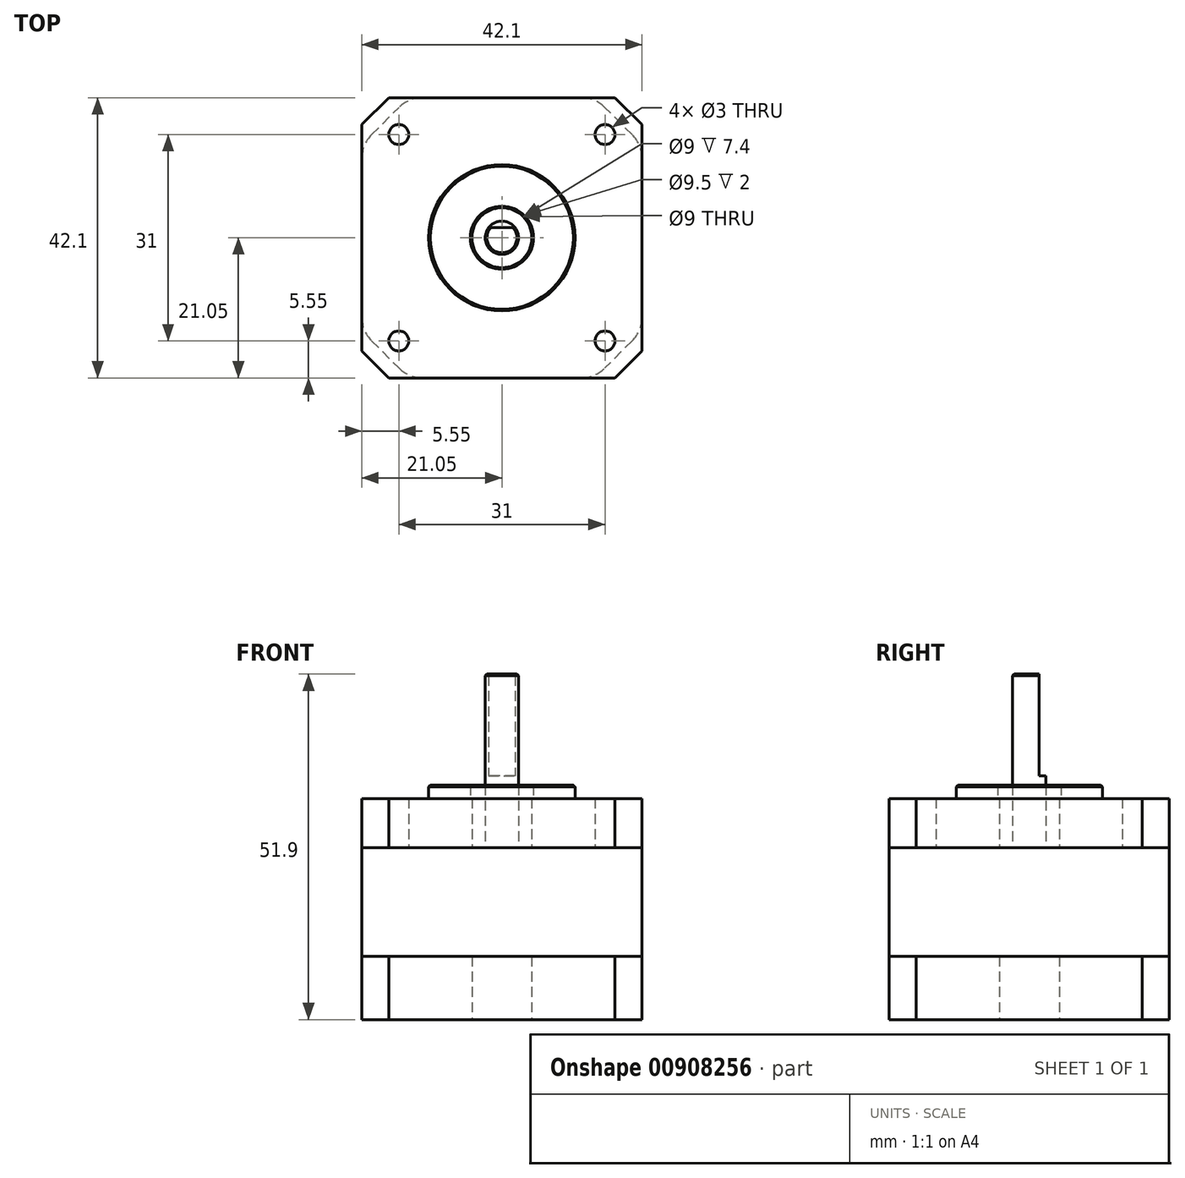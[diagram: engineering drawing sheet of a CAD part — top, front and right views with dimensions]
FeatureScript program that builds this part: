
annotation { "Feature Type Name" : "Feature", "Feature Type Description" : "" }
export const myFeature = defineFeature(function(context is Context, id is Id, definition is map)
    precondition{}
    {
        {
            var Q0;
            Q0=qCreatedBy(makeId("Top.planeOp"),FACE);
            var sketch = newSketch(context, id + "F0", { "sketchPlane" : qUnion([Q0])});
            skPoint(sketch, "E0.middle", {"position": v(0, 0) * mm});
            skLineSegment(sketch, "E1", {"start": v(0, 21.05) * mm, "end": v(17, 21.05) * mm});
            skLineSegment(sketch, "E2", {"start": v(17, 21.05) * mm, "end": v(21.05, 17) * mm});
            skLineSegment(sketch, "E3", {"start": v(21.05, 17) * mm, "end": v(21.05, 0) * mm});
            skLineSegment(sketch, "E4.MirrorCS", {"start": v(0, 21.05) * mm, "end": v(-17, 21.05) * mm});
            skLineSegment(sketch, "E5.MirrorCS", {"start": v(-21.05, 17) * mm, "end": v(-21.05, 0) * mm});
            skLineSegment(sketch, "E6.MirrorCS", {"start": v(-17, 21.05) * mm, "end": v(-21.05, 17) * mm});
            skLineSegment(sketch, "E7.MirrorCS", {"start": v(21.05, -17) * mm, "end": v(21.05, 0) * mm});
            skLineSegment(sketch, "E8.MirrorCS", {"start": v(17, -21.05) * mm, "end": v(21.05, -17) * mm});
            skLineSegment(sketch, "E9.MirrorCS", {"start": v(0, -21.05) * mm, "end": v(17, -21.05) * mm});
            skLineSegment(sketch, "E10.MirrorCS", {"start": v(0, -21.05) * mm, "end": v(-17, -21.05) * mm});
            skLineSegment(sketch, "E11.MirrorCS", {"start": v(-17, -21.05) * mm, "end": v(-21.05, -17) * mm});
            skLineSegment(sketch, "E12.MirrorCS", {"start": v(-21.05, -17) * mm, "end": v(-21.05, 0) * mm});
            skCircle(sketch, "E13", {"center": v(0, 0) * mm, "radius": 4.5 * mm});
            skSolve(sketch);
        }
        {
            var Q0;
            Q0 = qSketchRegion(id + "F0", true);
            extrude(context, id + "F1", {"entities" : qUnion([Q0]), "depth" : 9.5 * mm, "offsetDistance" : 25 * mm});
        }
        {
            var Q0;
            Q0=makeQuery(id+"F1.opExtrude","CAP_FACE",FACE,{"disambiguationData":[OSD([sQuery(id+"F0.wireOp",EDGE,"E1"),sQuery(id+"F0.wireOp",EDGE,"E4.MirrorCS"),sQuery(id+"F0.wireOp",EDGE,"E5.MirrorCS"),sQuery(id+"F0.wireOp",EDGE,"E6.MirrorCS"),sQuery(id+"F0.wireOp",EDGE,"E2"),sQuery(id+"F0.wireOp",EDGE,"E3"),sQuery(id+"F0.wireOp",EDGE,"E7.MirrorCS"),sQuery(id+"F0.wireOp",EDGE,"E8.MirrorCS"),sQuery(id+"F0.wireOp",EDGE,"E9.MirrorCS"),sQuery(id+"F0.wireOp",EDGE,"E10.MirrorCS"),sQuery(id+"F0.wireOp",EDGE,"E11.MirrorCS"),sQuery(id+"F0.wireOp",EDGE,"E12.MirrorCS"),sQuery(id+"F0.wireOp",EDGE,"E13")])],"isStart":false});
            var sketch = newSketch(context, id + "F2", { "sketchPlane" : qUnion([Q0])});
            skLineSegment(sketch, "E14", {"start": v(-21.05, 0) * mm, "end": v(-21.05, 14) * mm});
            skLineSegment(sketch, "E15", {"start": v(-21.05, 14) * mm, "end": v(-14, 21.05) * mm});
            skLineSegment(sketch, "E16", {"start": v(-14, 21.05) * mm, "end": v(0, 21.05) * mm});
            skLineSegment(sketch, "E17.MirrorCS", {"start": v(21.05, 0) * mm, "end": v(21.05, 14) * mm});
            skLineSegment(sketch, "E18.MirrorCS", {"start": v(21.05, 14) * mm, "end": v(14, 21.05) * mm});
            skLineSegment(sketch, "E19.MirrorCS", {"start": v(14, 21.05) * mm, "end": v(0, 21.05) * mm});
            skLineSegment(sketch, "E20.MirrorCS", {"start": v(21.05, 0) * mm, "end": v(21.05, -14) * mm});
            skLineSegment(sketch, "E21.MirrorCS", {"start": v(21.05, -14) * mm, "end": v(14, -21.05) * mm});
            skLineSegment(sketch, "E22.MirrorCS", {"start": v(14, -21.05) * mm, "end": v(0, -21.05) * mm});
            skLineSegment(sketch, "E23.MirrorCS", {"start": v(-14, -21.05) * mm, "end": v(0, -21.05) * mm});
            skLineSegment(sketch, "E24.MirrorCS", {"start": v(-21.05, -14) * mm, "end": v(-14, -21.05) * mm});
            skLineSegment(sketch, "E25.MirrorCS", {"start": v(-21.05, 0) * mm, "end": v(-21.05, -14) * mm});
            skSolve(sketch);
        }
        {
            var Q0;
            Q0 = qSketchRegion(id + "F2", true);
            extrude(context, id + "F3", {"entities" : qUnion([Q0]), "depth" : 16.3 * mm, "offsetDistance" : 25 * mm});
        }
        {
            var Q0;
            Q0=makeQuery(id+"F3.opExtrude","CAP_FACE",FACE,{"disambiguationData":[OSD([sQuery(id+"F2.wireOp",EDGE,"E14"),sQuery(id+"F2.wireOp",EDGE,"E15"),sQuery(id+"F2.wireOp",EDGE,"E16"),sQuery(id+"F2.wireOp",EDGE,"E17.MirrorCS"),sQuery(id+"F2.wireOp",EDGE,"E18.MirrorCS"),sQuery(id+"F2.wireOp",EDGE,"E19.MirrorCS"),sQuery(id+"F2.wireOp",EDGE,"E20.MirrorCS"),sQuery(id+"F2.wireOp",EDGE,"E21.MirrorCS"),sQuery(id+"F2.wireOp",EDGE,"E22.MirrorCS"),sQuery(id+"F2.wireOp",EDGE,"E23.MirrorCS"),sQuery(id+"F2.wireOp",EDGE,"E24.MirrorCS"),sQuery(id+"F2.wireOp",EDGE,"E25.MirrorCS")])],"isStart":false});
            var sketch = newSketch(context, id + "F4", { "sketchPlane" : qUnion([Q0])});
            skPoint(sketch, "E26.middle", {"position": v(0, 0) * mm});
            skLineSegment(sketch, "E27", {"start": v(0, 21.05) * mm, "end": v(17, 21.05) * mm});
            skLineSegment(sketch, "E28", {"start": v(17, 21.05) * mm, "end": v(21.05, 17) * mm});
            skLineSegment(sketch, "E29", {"start": v(21.05, 17) * mm, "end": v(21.05, 0) * mm});
            skLineSegment(sketch, "E30.MirrorCS", {"start": v(0, 21.05) * mm, "end": v(-17, 21.05) * mm});
            skLineSegment(sketch, "E31.MirrorCS", {"start": v(-21.05, 17) * mm, "end": v(-21.05, 0) * mm});
            skLineSegment(sketch, "E32.MirrorCS", {"start": v(-17, 21.05) * mm, "end": v(-21.05, 17) * mm});
            skLineSegment(sketch, "E33.MirrorCS", {"start": v(21.05, -17) * mm, "end": v(21.05, 0) * mm});
            skLineSegment(sketch, "E34.MirrorCS", {"start": v(17, -21.05) * mm, "end": v(21.05, -17) * mm});
            skLineSegment(sketch, "E35.MirrorCS", {"start": v(0, -21.05) * mm, "end": v(17, -21.05) * mm});
            skLineSegment(sketch, "E36.MirrorCS", {"start": v(0, -21.05) * mm, "end": v(-17, -21.05) * mm});
            skLineSegment(sketch, "E37.MirrorCS", {"start": v(-17, -21.05) * mm, "end": v(-21.05, -17) * mm});
            skLineSegment(sketch, "E38.MirrorCS", {"start": v(-21.05, -17) * mm, "end": v(-21.05, 0) * mm});
            skCircle(sketch, "E39", {"center": v(0, 0) * mm, "radius": 4.5 * mm});
            skCircle(sketch, "E40", {"center": v(15.5, 15.5) * mm, "radius": 1.5 * mm});
            skCircle(sketch, "E41.MirrorC", {"center": v(-15.5, 15.5) * mm, "radius": 1.5 * mm});
            skCircle(sketch, "E42.MirrorC", {"center": v(15.5, -15.5) * mm, "radius": 1.5 * mm});
            skCircle(sketch, "E43.MirrorC", {"center": v(-15.5, -15.5) * mm, "radius": 1.5 * mm});
            skSolve(sketch);
        }
        {
            var Q0;
            Q0 = qSketchRegion(id + "F4", true);
            extrude(context, id + "F5", {"entities" : qUnion([Q0]), "depth" : 7.4 * mm, "offsetDistance" : 25 * mm});
        }
        {
            var Q0;
            Q0=makeQuery(id+"F5.opExtrude","CAP_FACE",FACE,{"disambiguationData":[OSD([sQuery(id+"F4.wireOp",EDGE,"E27"),sQuery(id+"F4.wireOp",EDGE,"E30.MirrorCS"),sQuery(id+"F4.wireOp",EDGE,"E31.MirrorCS"),sQuery(id+"F4.wireOp",EDGE,"E32.MirrorCS"),sQuery(id+"F4.wireOp",EDGE,"E28"),sQuery(id+"F4.wireOp",EDGE,"E29"),sQuery(id+"F4.wireOp",EDGE,"E33.MirrorCS"),sQuery(id+"F4.wireOp",EDGE,"E34.MirrorCS"),sQuery(id+"F4.wireOp",EDGE,"E35.MirrorCS"),sQuery(id+"F4.wireOp",EDGE,"E36.MirrorCS"),sQuery(id+"F4.wireOp",EDGE,"E37.MirrorCS"),sQuery(id+"F4.wireOp",EDGE,"E38.MirrorCS"),sQuery(id+"F4.wireOp",EDGE,"E39"),sQuery(id+"F4.wireOp",EDGE,"E40"),sQuery(id+"F4.wireOp",EDGE,"E41.MirrorC"),sQuery(id+"F4.wireOp",EDGE,"E42.MirrorC"),sQuery(id+"F4.wireOp",EDGE,"E43.MirrorC")])],"isStart":false});
            var sketch = newSketch(context, id + "F6", { "sketchPlane" : qUnion([Q0])});
            skCircle(sketch, "E44", {"center": v(0, 0) * mm, "radius": 11 * mm});
            skCircle(sketch, "E45", {"center": v(0, 0) * mm, "radius": 4.75 * mm});
            skSolve(sketch);
        }
        {
            var Q0;
            Q0 = qSketchRegion(id + "F6", true);
            extrude(context, id + "F7", {"entities" : qUnion([Q0]), "operationType" : NewBodyOperationType.ADD, "depth" : 2 * mm, "offsetDistance" : 25 * mm});
        }
        {
            var Q0;
            Q0=makeQuery(id+"F7.opExtrude","CAP_EDGE",EDGE,{"disambiguationData":[OSD([sQuery(id+"F6.wireOp",EDGE,"E44")])],"isStart":false});
            chamfer(context, id + "F8", {"entities" : qUnion([Q0]), "width" : 0.25 * mm, "tangentPropagation" : true});
        }
        {
            var Q0;
            Q0=makeQuery(id+"F3.opExtrude","CAP_FACE",FACE,{"disambiguationData":[OSD([sQuery(id+"F2.wireOp",EDGE,"E14"),sQuery(id+"F2.wireOp",EDGE,"E15"),sQuery(id+"F2.wireOp",EDGE,"E16"),sQuery(id+"F2.wireOp",EDGE,"E17.MirrorCS"),sQuery(id+"F2.wireOp",EDGE,"E18.MirrorCS"),sQuery(id+"F2.wireOp",EDGE,"E19.MirrorCS"),sQuery(id+"F2.wireOp",EDGE,"E20.MirrorCS"),sQuery(id+"F2.wireOp",EDGE,"E21.MirrorCS"),sQuery(id+"F2.wireOp",EDGE,"E22.MirrorCS"),sQuery(id+"F2.wireOp",EDGE,"E23.MirrorCS"),sQuery(id+"F2.wireOp",EDGE,"E24.MirrorCS"),sQuery(id+"F2.wireOp",EDGE,"E25.MirrorCS")])],"isStart":false});
            var sketch = newSketch(context, id + "F9", { "sketchPlane" : qUnion([Q0])});
            skCircle(sketch, "E46", {"center": v(0, 0) * mm, "radius": 2.5 * mm});
            skSolve(sketch);
        }
        {
            var Q0;
            Q0 = qSketchRegion(id + "F9", true);
            extrude(context, id + "F10", {"entities" : qUnion([Q0]), "depth" : 26.1 * mm, "offsetDistance" : 25 * mm});
        }
        {
            var Q0;
            Q0=makeQuery(id+"F10.opExtrude","CAP_EDGE",EDGE,{"disambiguationData":[OSD([sQuery(id+"F9.wireOp",EDGE,"E46")])],"isStart":false});
            chamfer(context, id + "F11", {"entities" : qUnion([Q0]), "width" : 0.25 * mm, "tangentPropagation" : true});
        }
        {
            var Q0;
            Q0=makeQuery(id+"F10.opExtrude","CAP_FACE",FACE,{"disambiguationData":[OSD([sQuery(id+"F9.wireOp",EDGE,"E46")])],"isStart":false});
            var sketch = newSketch(context, id + "F12", { "sketchPlane" : qUnion([Q0])});
            skLineSegment(sketch, "E47.bottom", {"start": v(-3.24, 3.4) * mm, "end": v(3.22, 3.4) * mm});
            skLineSegment(sketch, "E47.top", {"start": v(-3.24, 1.5) * mm, "end": v(3.22, 1.5) * mm});
            skLineSegment(sketch, "E47.left", {"start": v(-3.24, 3.4) * mm, "end": v(-3.24, 1.5) * mm});
            skLineSegment(sketch, "E47.right", {"start": v(3.22, 3.4) * mm, "end": v(3.22, 1.5) * mm});
            skSolve(sketch);
        }
        {
            var Q0;
            Q0 = qSketchRegion(id + "F12", true);
            extrude(context, id + "F13", {"entities" : qUnion([Q0]), "operationType" : NewBodyOperationType.REMOVE, "oppositeDirection" : true, "depth" : 15.3 * mm, "offsetDistance" : 25 * mm});
        }
        {
            var Q0;
            Q0=makeQuery(id+"F3.opExtrude","SWEPT_EDGE",EDGE,{"disambiguationData":[OSD([sQuery(id+"F0.wireOp",EDGE,"E1"),sQuery(id+"F0.wireOp",EDGE,"E4.MirrorCS"),sQuery(id+"F2.wireOp",EDGE,"E18.MirrorCS"),sQuery(id+"F2.wireOp",EDGE,"E19.MirrorCS")])]});
            var Q1;
            Q1=makeQuery(id+"F3.opExtrude","SWEPT_EDGE",EDGE,{"disambiguationData":[OSD([sQuery(id+"F0.wireOp",EDGE,"E3"),sQuery(id+"F0.wireOp",EDGE,"E7.MirrorCS"),sQuery(id+"F2.wireOp",EDGE,"E17.MirrorCS"),sQuery(id+"F2.wireOp",EDGE,"E18.MirrorCS")])]});
            var Q2;
            Q2=makeQuery(id+"F3.opExtrude","SWEPT_EDGE",EDGE,{"disambiguationData":[OSD([sQuery(id+"F0.wireOp",EDGE,"E3"),sQuery(id+"F0.wireOp",EDGE,"E7.MirrorCS"),sQuery(id+"F2.wireOp",EDGE,"E20.MirrorCS"),sQuery(id+"F2.wireOp",EDGE,"E21.MirrorCS")])]});
            var Q3;
            Q3=makeQuery(id+"F3.opExtrude","SWEPT_EDGE",EDGE,{"disambiguationData":[OSD([sQuery(id+"F0.wireOp",EDGE,"E9.MirrorCS"),sQuery(id+"F0.wireOp",EDGE,"E10.MirrorCS"),sQuery(id+"F2.wireOp",EDGE,"E21.MirrorCS"),sQuery(id+"F2.wireOp",EDGE,"E22.MirrorCS")])]});
            var Q4;
            Q4=makeQuery(id+"F3.opExtrude","SWEPT_EDGE",EDGE,{"disambiguationData":[OSD([sQuery(id+"F0.wireOp",EDGE,"E9.MirrorCS"),sQuery(id+"F0.wireOp",EDGE,"E10.MirrorCS"),sQuery(id+"F2.wireOp",EDGE,"E23.MirrorCS"),sQuery(id+"F2.wireOp",EDGE,"E24.MirrorCS")])]});
            var Q5;
            Q5=makeQuery(id+"F3.opExtrude","SWEPT_EDGE",EDGE,{"disambiguationData":[OSD([sQuery(id+"F0.wireOp",EDGE,"E5.MirrorCS"),sQuery(id+"F0.wireOp",EDGE,"E12.MirrorCS"),sQuery(id+"F2.wireOp",EDGE,"E24.MirrorCS"),sQuery(id+"F2.wireOp",EDGE,"E25.MirrorCS")])]});
            var Q6;
            Q6=makeQuery(id+"F3.opExtrude","SWEPT_EDGE",EDGE,{"disambiguationData":[OSD([sQuery(id+"F0.wireOp",EDGE,"E5.MirrorCS"),sQuery(id+"F0.wireOp",EDGE,"E12.MirrorCS"),sQuery(id+"F2.wireOp",EDGE,"E14"),sQuery(id+"F2.wireOp",EDGE,"E15")])]});
            var Q7;
            Q7=makeQuery(id+"F3.opExtrude","SWEPT_EDGE",EDGE,{"disambiguationData":[OSD([sQuery(id+"F0.wireOp",EDGE,"E1"),sQuery(id+"F0.wireOp",EDGE,"E4.MirrorCS"),sQuery(id+"F2.wireOp",EDGE,"E15"),sQuery(id+"F2.wireOp",EDGE,"E16")])]});
            fillet(context, id + "F14", {"entities" : qUnion([Q0, Q1, Q2, Q3, Q4, Q5, Q6, Q7]), "radius" : 5 * mm, "tangentPropagation" : true, "allowEdgeOverflow" : false});
        }
    });
